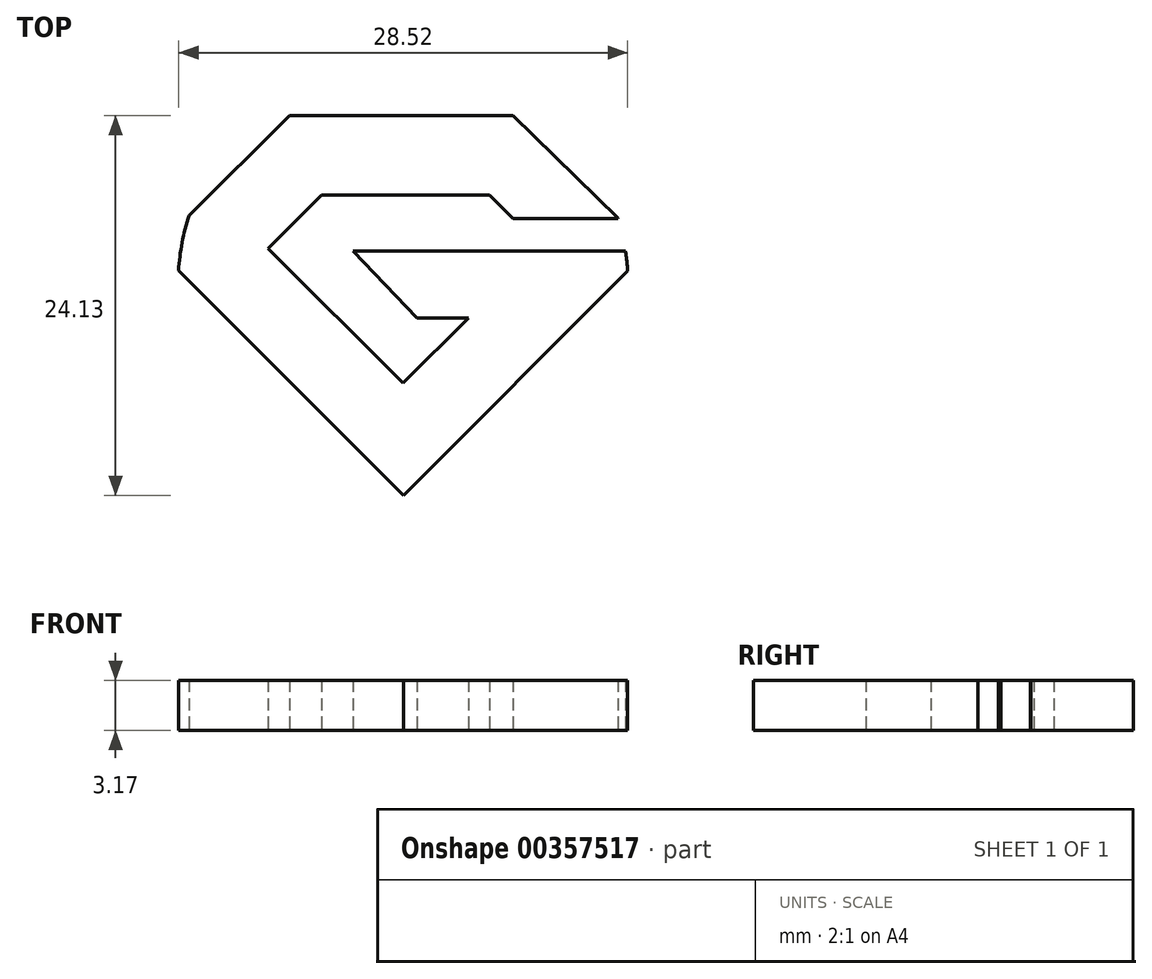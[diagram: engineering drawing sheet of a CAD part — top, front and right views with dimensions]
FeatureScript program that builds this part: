
annotation { "Feature Type Name" : "Feature", "Feature Type Description" : "" }
export const myFeature = defineFeature(function(context is Context, id is Id, definition is map)
    precondition{}
    {
        {
            var Q0;
            Q0=qCreatedBy(makeId("Top.planeOp"),FACE);
            var sketch = newSketch(context, id + "F0", { "sketchPlane" : qUnion([Q0])});
            skLineSegment(sketch, "E0", {"start": v(-47.35, -7.5) * mm, "end": v(-33.15, -7.5) * mm});
            skLineSegment(sketch, "E1", {"start": v(-33.15, -7.5) * mm, "end": v(-26.44, -14.05) * mm});
            skLineSegment(sketch, "E2", {"start": v(-26.44, -14.05) * mm, "end": v(-33.15, -14.05) * mm});
            skLineSegment(sketch, "E3", {"start": v(-33.15, -14.05) * mm, "end": v(-34.65, -12.55) * mm});
            skLineSegment(sketch, "E4", {"start": v(-34.65, -12.55) * mm, "end": v(-45.3, -12.55) * mm});
            skLineSegment(sketch, "E5", {"start": v(-45.3, -12.55) * mm, "end": v(-48.7, -15.94) * mm});
            skLineSegment(sketch, "E6", {"start": v(-48.7, -15.94) * mm, "end": v(-40.13, -24.5) * mm});
            skLineSegment(sketch, "E7", {"start": v(-40.13, -24.5) * mm, "end": v(-36, -20.36) * mm});
            skLineSegment(sketch, "E8", {"start": v(-36, -20.36) * mm, "end": v(-39.26, -20.36) * mm});
            skLineSegment(sketch, "E9", {"start": v(-39.26, -20.36) * mm, "end": v(-43.32, -16.1) * mm});
            skLineSegment(sketch, "E10", {"start": v(-43.32, -16.1) * mm, "end": v(-24.58, -16.1) * mm});
            skLineSegment(sketch, "E11", {"start": v(-24.58, -16.1) * mm, "end": v(-40.1, -31.63) * mm});
            skLineSegment(sketch, "E12", {"start": v(-40.1, -31.63) * mm, "end": v(-55.82, -15.92) * mm});
            skLineSegment(sketch, "E13", {"start": v(-55.82, -15.92) * mm, "end": v(-47.35, -7.5) * mm});
            skCircle(sketch, "E14", {"center": v(-40.13, -18.23) * mm, "radius": 14.29 * mm});
            skPoint(sketch, "E14.centerSnap0", {"position": v(-41.3, -18.23) * mm});
            skSolve(sketch);
        }
        {
            var Q0;
            Q0=makeQuery(id+"F0.imprint","IMPRINT",FACE,{"disambiguationData":[TD([[makeQuery(id+"F0.imprint","IMPRINT",EDGE,{"derivedFrom":sQuery(id+"F0.wireOp",EDGE,"E0")}),-1.0]])]});
            extrude(context, id + "F1", {"entities" : qUnion([Q0]), "depth" : 3.17 * mm});
        }
    });
